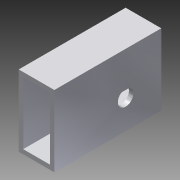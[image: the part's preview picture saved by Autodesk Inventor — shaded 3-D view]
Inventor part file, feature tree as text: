
AUTODESK INVENTOR PART (.ipt)
format: ipt  version: 2015 SP1 (Build 190203100, 203)  size: 110,080 bytes
history: native  units: in
note: dims shown in document units (in); Inventor stores cm internally (conversion verified against a paired STEP export)
features: sketch x2, extrude x1, hole x1
ambient origin geometry x8: Origin, YZ Plane, XZ Plane, XY Plane, X Axis, Y Axis, Z Axis, Center Point
bodies: Solid1 (feature_tree)
feature tree (4):
  extrude  "Extrusion1"  Depth=2.0in
  hole  "Hole1"  [1 undecoded]
  sketch  "Sketch1"  dims[d0=1.0in d1=2.0in]
  sketch  "Sketch2"  dims[d2=0.75in d3=1.75in d4=0.125in d5=0.125in d6=3.0in d7=0.0in d8=0.8125in d9=1.0in d10=0.4375in d11=0.75in d12=0.375in d13=0.25in d14=0.5635in d15=1.0in d16=0.8108in d17=1.0in d18=1.0in]
note: 1 required parameter value undecoded (feature->parameter linkage not recoverable at this tier; creation-order binding heuristic only, values carry confidence <= 0.55)
